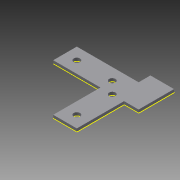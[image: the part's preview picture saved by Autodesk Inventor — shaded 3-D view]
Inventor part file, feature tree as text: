
AUTODESK INVENTOR PART (.ipt)
format: ipt  version: 2013 (Build 170138000, 138)  size: 117,760 bytes
history: native  units: in
note: dims shown in document units (in); Inventor stores cm internally (conversion verified against a paired STEP export)
features: sketch x3, extrude x2
ambient origin geometry x8: Origin, YZ Plane, XZ Plane, XY Plane, X Axis, Y Axis, Z Axis, Center Point
bodies: Solid1 (feature_tree)
feature tree (5):
  extrude  "Extrusion1"  Depth=1.0in
  extrude  "Extrusion2"  Depth=2.0in
  sketch  "Sketch3"  dims[d4=1.0in d5=0.266in d6=0.266in d7=0.266in d8=0.266in d9=0.5in d10=0.0in d11=0.5in d12=0.5in d13=0.5in d14=0.5in d15=0.5in d17=0.125in d18=0.0in d19=0.615in d20=1.5in d21=1.0in d22=0.125in d23=0.0in]
  sketch  "Sketch1"  dims[d0=3.0in d1=1.0in]
  sketch  "Sketch2"  dims[d2=2.0in d3=2.0in]
